# Revit family: MaviGard Gas Detectors
name_source: partatom
category: Fire Alarm Devices
units: mm (PartAtom-declared; Revit-internal decimal feet)

## family parameters
Cut with Voids When Loaded = No
Host = Face
Maintain Annotation Orientation = Yes
OmniClass Number = 23.85.30.21
OmniClass Title = Environmental Detection/Registration
Part Type = Normal
Room Calculation Point = No
Round Connector Dimension = Use Diameter
Shared = No

## types (13) — shared parameters
Code Performance = EN 50194-1
Color = White
Compatible sockets = ML-0120
Fax Number = (+)90 216 466 45 10
Installation Manual = https://mavilielektronik.com
Main Material = White Plastic PC/ABS
Manufacturer = Mavili Elektronik Ticaret A.Ş.
Model = MaviGard
Nominal Depth = 50 mm
Nominal Height = 100 mm
Nominal Width = 140 mm
Operating temperature = (-10°C) - (+55°C)
Protection Sign = IP42
Secondary Material = Plastic
URL = https://www.mavili.com.tr
Warranty Duration Labor = 2
Warranty Duration Parts = 2
Warranty Duration Unit = Year
zero-valued in all types: Cost, Default Elevation

## per-type parameters (varying)
| type | Description | Device Adress Setup | External supply | Mounting height | Mounting surface | Operating voltage range | Operatonal Voltage (default) | Product Code | Public Works Pose Number |
| MaviGard Carbon Monoxide Gas Detector (CO),12V DC, 2 Alarm Level Output, Electrochemical | Carbon Monoxide Gas Detector (CO),12V DC, 2 Alarm Level Output, Electrochemical |  | 24 V/DC | 150 cm | wall mount | 12-33V/DC | 12 V/DC | GD2R-12EC | 833-610 |
| MaviGard Carbon Monoxide Gas Detector (CO),24V DC, 2 Alarm Level Output, Electrochemical | Carbon Monoxide Gas Detector (CO),24V DC, 2 Alarm Level Output, Electrochemical |  | 24 V/DC | 150 cm | wall mount | 18-33V/DC | 24 V/DC | GD2R-24EC | 833-610 |
| MaviGard Carbon Monoxide Gas Detector (CO),220V AC, 2 Alarm Level Output, Electrochemical | Carbon Monoxide Gas Detector (CO),220V AC, 2 Alarm Level Output, Electrochemical |  | 220 V/AC | 150 cm | wall mount | 18-33V/DC | 24 V/DC | GD2R-220EC | 833-610 |
| MaviGard Gas Detector For LPG, 12/24V DC, With Relay Output | Gas Detector For LPG, 12/24V DC, With Relay Output |  | 24 V/DC | 15-25 cm above from ground | wall mount | 18-33V/DC | 24 V/DC | GDR-1224L | 833-606 |
| MaviGard Gas Detector For LPG, 220V AC, With Relay Output | Gas Detector For LPG, 220V AC, With Relay Output |  | 220 V/DC | 15-25 cm above from ground | Wall mount | 18-33V/DC | 24 V/DC | GDR-220L | 833-606 |
| MaviGard Gas Detector For Methane, 12/24V DC, With Relay Output | Gas Detector For Methane, 12/24V DC, With Relay Output |  | 24 V/DC | 15-25 cm below the ceiling | wall mount | 12-33V/DC | 24 V/DC | GDR-1224M | 833-608 |
| MaviGard Gas Detector For Methane, 220V AC With Relay Output | Gas Detector For Methane, 220V AC With Relay Output |  | 220 V/AC | 15-25 cm below the ceiling | wall mount | 18-33V/DC | 24 V/DC | GDR-220M | 833-608 |
| MaviGard Intelligent Addressabe Gas Detector For Carbon Monoxide, 24V DC, Electrochemical | Intelligent Addressabe Gas Detector For Carbon Monoxide, 24V DC, Electrochemical | The address is given to devices by addressable programmer | 24 V/DC | 150 cm | wall mount | 12-33V/DC | 24 V/DC | AGD-1224EC.VIP |  |
| MaviGard Intelligent Addressabe Gas Detector For Carbon Monoxide, 220V AC, Electrochemical | Intelligent Addressabe Gas Detector For Carbon Monoxide, 220V AC, Electrochemical | The address is given to devices by addressable programmer | 220 V/AC | 150 cm | wall mount | 12-33V/DC | 24 V/DC | AGD-220EC.VIP |  |
| MaviGard Intelligent Addressabe Gas Detector For LPG, 24V DC | Intelligent Addressabe Gas Detector For LPG, 24V DC | The address is given to devices by addressable programmer | 24 V/DC | 15-25 cm above from ground | wall mount | 12-33V/DC | 24 V/DC | AGD-1224L.VIP | 833-605 |
| MaviGard Intelligent Addressabe LPG (Buthane + Propane)  Detector, 220V AC | Intelligent Addressabe LPG (Buthane + Propane)  Detector, 220V AC | The address is given to devices by addressable programmer | 220 V/AC | 15-25 cm above from ground | wall mount | 12-33V/DC | 24 V/DC | AGD-220L.VIP |  |
| MaviGard Intelligent Addressabe Gas Detector For Methane, 24V DC | Intelligent Addressabe Gas Detector For Methane, 24V DC | The address is given to devices by addressable programmer | 24 V/DC | 15-25 cm below the ceiling | wall mount | 12-33V/DC | 24 V/DC | AGD-1224M.VIP | 833-607 |
| MaviGard Intelligent Addressabe Gas Detector For Methane, 220V AC | Intelligent Addressabe Gas Detector For Methane, 220V AC | The address is given to devices by addressable programmer | 220 V/AC | 15-25 cm below the ceiling | wall mount | 12-33V/DC | 24 V/DC | AGD-220M.VIP |  |

## geometry (parser evidence)
native form markers: Sweep x1
no freeform markers — native parametric forms only
